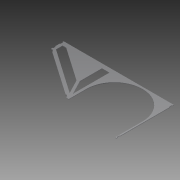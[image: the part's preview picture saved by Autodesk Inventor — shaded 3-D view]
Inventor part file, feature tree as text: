
AUTODESK INVENTOR PART (.ipt)
format: ipt  version: 2013 (Build 170138000, 138)  size: 139,264 bytes
history: native  units: in
note: dims shown in document units (in); Inventor stores cm internally (conversion verified against a paired STEP export)
features: extrude x4, sketch x4
ambient origin geometry x8: Origin, YZ Plane, XZ Plane, XY Plane, X Axis, Y Axis, Z Axis, Center Point
feature tree (8):
  extrude  "Extrusion2"  Depth=12.0in
  extrude  "Extrusion3"  Depth=5.75in
  extrude  "Extrusion4"  Depth=11.5in
  extrude  "Extrusion5"  Depth=0.25in
  sketch  "Sketch1"  dims[d0=22.0in d2=12.0in]
  sketch  "Sketch2"  dims[d3=11.25in d5=5.75in]
  sketch  "Sketch3"  dims[d8=0.125in d9=0.0in d10=11.5in]
  sketch  "Sketch4"  dims[d14=2.5in d15=0.25in d16=0.5in d17=0.5in d18=0.25in d19=0.125in d20=0.0in d21=0.5in d22=0.25in d23=0.25in d24=0.5in d25=0.125in d26=0.0in d27=0.5in d28=0.5in d29=0.25in d30=10.0in d31=0.125in d32=0.0in d33=9.5in d34=5.5in d37=0.25in]
